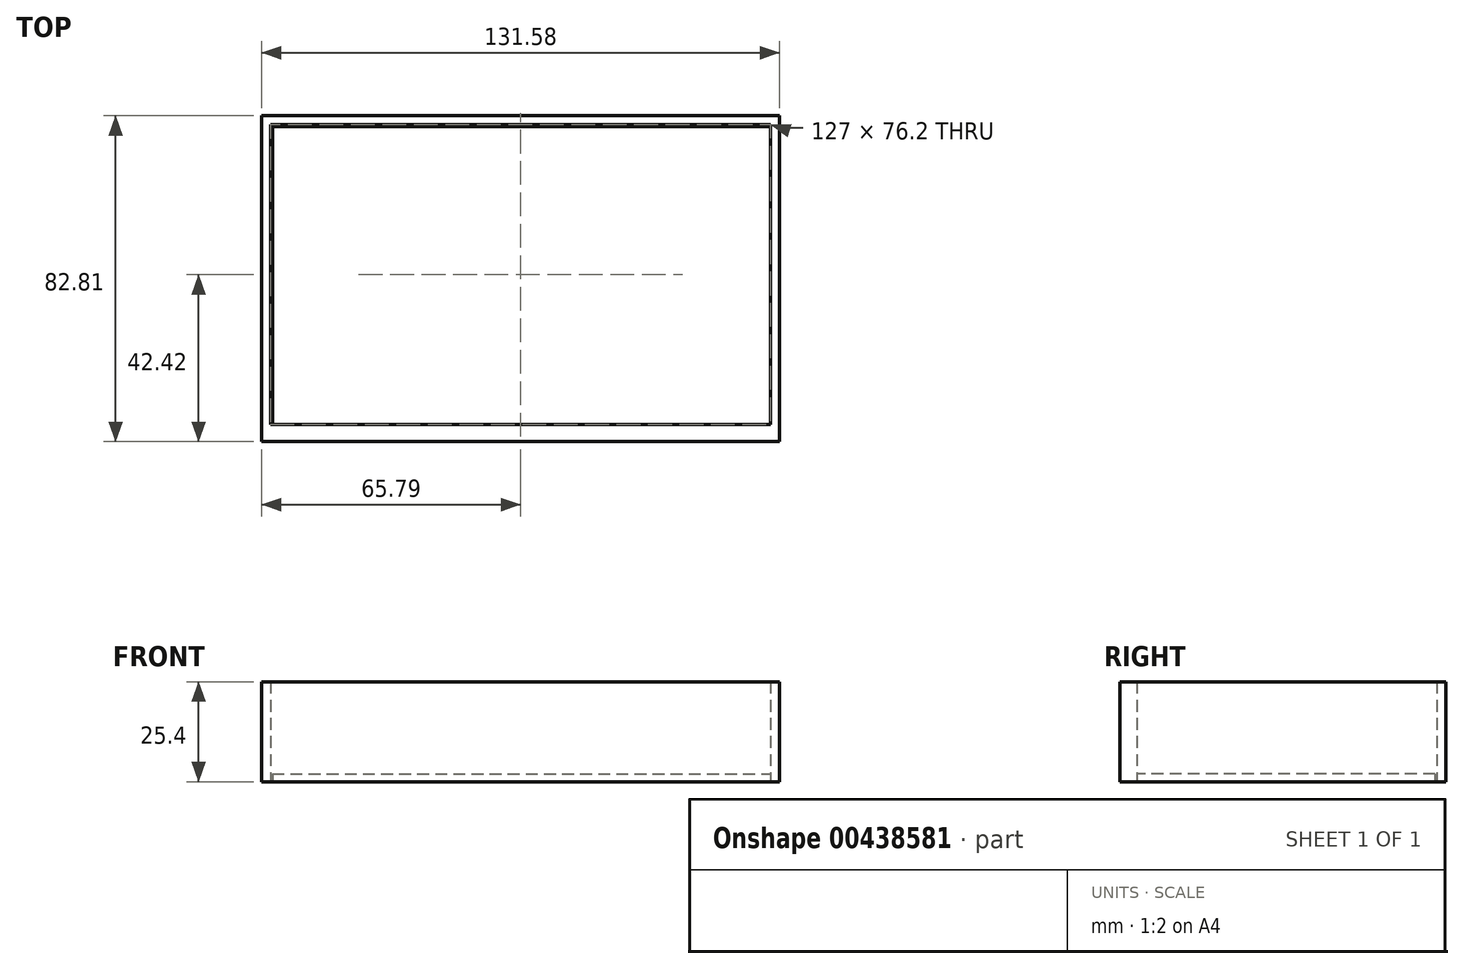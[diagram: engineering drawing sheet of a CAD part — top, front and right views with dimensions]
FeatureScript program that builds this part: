
annotation { "Feature Type Name" : "Feature", "Feature Type Description" : "" }
export const myFeature = defineFeature(function(context is Context, id is Id, definition is map)
    precondition{}
    {
        {
            var Q0;
            Q0=qCreatedBy(makeId("Top.planeOp"),FACE);
            var sketch = newSketch(context, id + "F0", { "sketchPlane" : qUnion([Q0])});
            skLineSegment(sketch, "E0.bottom", {"start": v(-63.5, 38.1) * mm, "end": v(63.5, 38.1) * mm});
            skLineSegment(sketch, "E0.top", {"start": v(-63.5, -38.1) * mm, "end": v(63.5, -38.1) * mm});
            skLineSegment(sketch, "E0.left", {"start": v(-63.5, 38.1) * mm, "end": v(-63.5, -38.1) * mm});
            skLineSegment(sketch, "E0.right", {"start": v(63.5, 38.1) * mm, "end": v(63.5, -38.1) * mm});
            skPoint(sketch, "E0.middle", {"position": v(0, 0) * mm});
            skLineSegment(sketch, "E1.0", {"start": v(65.79, 40.39) * mm, "end": v(65.79, -40.39) * mm});
            skLineSegment(sketch, "E1.1", {"start": v(-65.79, 40.39) * mm, "end": v(65.79, 40.39) * mm});
            skLineSegment(sketch, "E1.2", {"start": v(-65.79, 40.39) * mm, "end": v(-65.79, -40.39) * mm});
            skLineSegment(sketch, "E1.3", {"start": v(-65.79, -40.39) * mm, "end": v(65.79, -40.39) * mm});
            skSolve(sketch);
        }
        {
            var Q0;
            Q0=makeQuery(id+"F0.imprint","IMPRINT",FACE,{"disambiguationData":[TD([[makeQuery(id+"F0.imprint","IMPRINT",EDGE,{"derivedFrom":sQuery(id+"F0.wireOp",EDGE,"E0.bottom")}),1.0]])]});
            extrude(context, id + "F1", {"entities" : qUnion([Q0]), "depth" : 25.4 * mm});
        }
        {
            var Q0;
            Q0=qCreatedBy(makeId("Top.planeOp"),FACE);
            var sketch = newSketch(context, id + "F2", { "sketchPlane" : qUnion([Q0])});
            skLineSegment(sketch, "E2.bottom", {"start": v(-63.05, 37.66) * mm, "end": v(63.48, 37.66) * mm});
            skLineSegment(sketch, "E2.top", {"start": v(-63.05, -38.11) * mm, "end": v(63.48, -38.11) * mm});
            skLineSegment(sketch, "E2.left", {"start": v(-63.05, 37.66) * mm, "end": v(-63.05, -38.11) * mm});
            skLineSegment(sketch, "E2.right", {"start": v(63.48, 37.66) * mm, "end": v(63.48, -38.11) * mm});
            skSolve(sketch);
        }
        {
            var Q0;
            Q0=makeQuery(id+"F1.opExtrude","SWEPT_FACE",FACE,{"disambiguationData":[OSD([sQuery(id+"F0.wireOp",EDGE,"E1.3")])]});
            extrude(context, id + "F3", {"entities" : qUnion([Q0]), "operationType" : NewBodyOperationType.ADD, "depth" : 2.03 * mm});
        }
        {
            var Q0;
            Q0=makeQuery(id+"F2.imprint","IMPRINT",FACE,{"disambiguationData":[TD([[makeQuery(id+"F2.imprint","IMPRINT",EDGE,{"derivedFrom":sQuery(id+"F2.wireOp",EDGE,"E2.bottom")}),-1.0]])]});
            extrude(context, id + "F4", {"entities" : qUnion([Q0]), "operationType" : NewBodyOperationType.ADD, "depth" : 2.03 * mm});
        }
    });
